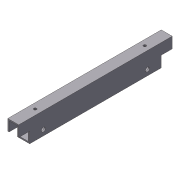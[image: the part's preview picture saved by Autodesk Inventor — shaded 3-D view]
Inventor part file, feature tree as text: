
AUTODESK INVENTOR PART (.ipt)
format: ipt  version: 2012 (Build 160160000, 160)  size: 116,224 bytes
history: native  units: in
note: dims shown in document units (in); Inventor stores cm internally (conversion verified against a paired STEP export)
features: extrude x4, sketch x4, shell x1
ambient origin geometry x8: Origin, YZ Plane, XZ Plane, XY Plane, X Axis, Y Axis, Z Axis, Center Point
bodies: Solid1 (feature_tree)
feature tree (9):
  extrude  "Extrusion1"  Depth=2.0in
  shell  "Shell1"  Thickness=14.0in
  extrude  "Extrusion2"  Depth=1.0in
  extrude  "Extrusion3"  Depth=0.375in
  extrude  "Extrusion4"  Depth=0.5in
  sketch  "Sketch1"  dims[d0=1.0in d1=2.0in d2=14.0in d3=0.0in]
  sketch  "Sketch2"  dims[d4=0.125in d5=1.0in]
  sketch  "Sketch3"  dims[d6=14.0in d7=0.0in d8=0.375in]
  sketch  "Sketch4"  dims[d9=1.25in d10=0.5in d11=0.5in d12=1.25in d13=14.0in d14=0.0in d15=0.25in d16=0.5in d17=2.0in d18=10.0in d19=2.0in d20=1.0in d21=0.0in]
